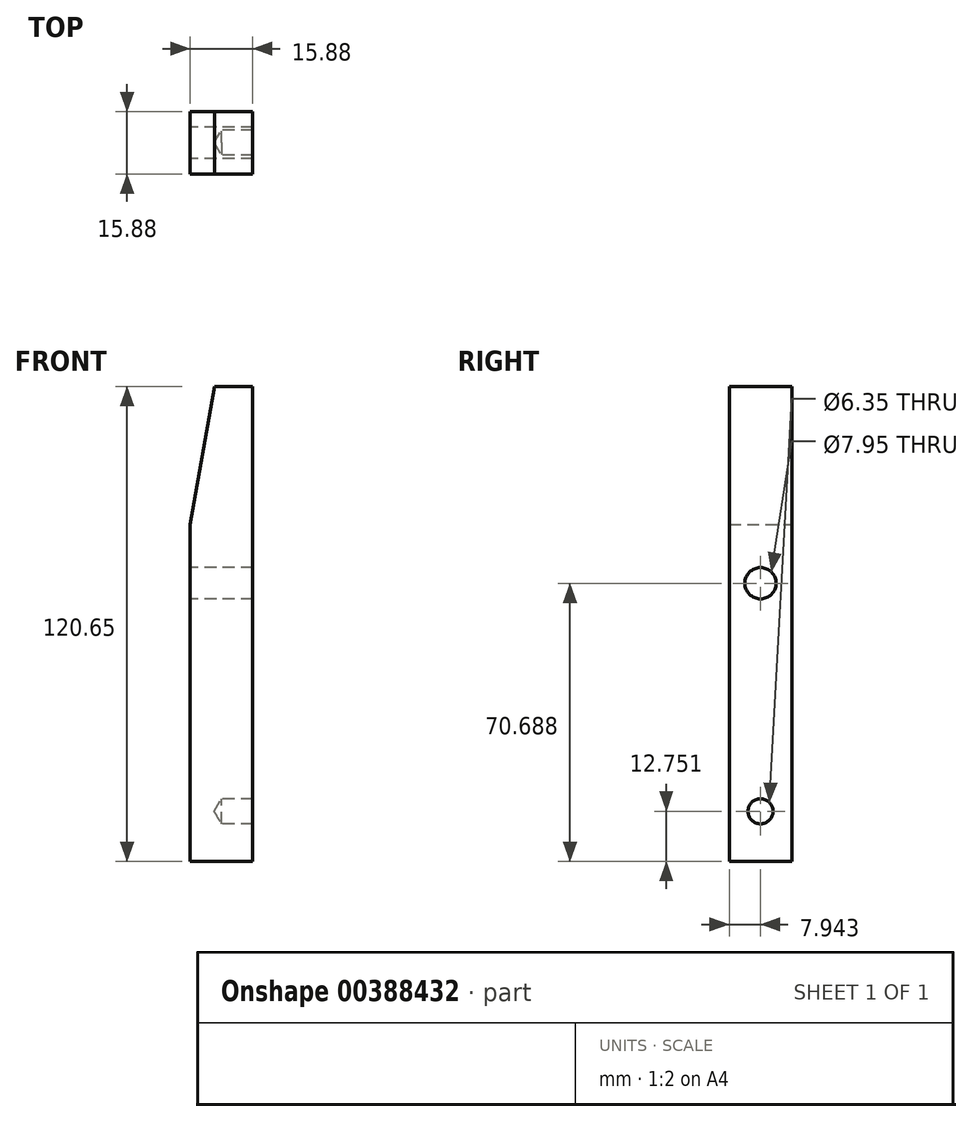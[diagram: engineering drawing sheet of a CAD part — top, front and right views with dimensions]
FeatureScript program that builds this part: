
annotation { "Feature Type Name" : "Feature", "Feature Type Description" : "" }
export const myFeature = defineFeature(function(context is Context, id is Id, definition is map)
    precondition{}
    {
        {
            var Q0;
            Q0=qCreatedBy(makeId("Front.planeOp"),FACE);
            var sketch = newSketch(context, id + "F0", { "sketchPlane" : qUnion([Q0])});
            skLineSegment(sketch, "E0", {"start": v(0, 0) * mm, "end": v(0, 85.6) * mm});
            skLineSegment(sketch, "E1", {"start": v(0, 85.6) * mm, "end": v(6.17, 120.65) * mm});
            skLineSegment(sketch, "E2", {"start": v(6.17, 120.65) * mm, "end": v(15.87, 120.65) * mm});
            skLineSegment(sketch, "E3", {"start": v(15.87, 120.65) * mm, "end": v(15.88, 0) * mm});
            skLineSegment(sketch, "E4", {"start": v(15.88, 0) * mm, "end": v(0, 0) * mm});
            skSolve(sketch);
        }
        {
            var Q0;
            Q0=makeQuery(id+"F0.imprint","IMPRINT",FACE,{"disambiguationData":[TD([[makeQuery(id+"F0.imprint","IMPRINT",EDGE,{"derivedFrom":sQuery(id+"F0.wireOp",EDGE,"E0")}),-1.0]])]});
            extrude(context, id + "F1", {"entities" : qUnion([Q0]), "depth" : 15.88 * mm});
        }
        {
            var Q0;
            Q0=makeQuery(id+"F1.opExtrude","SWEPT_FACE",FACE,{"disambiguationData":[OSD([sQuery(id+"F0.wireOp",EDGE,"E3")])]});
            var sketch = newSketch(context, id + "F2", { "sketchPlane" : qUnion([Q0])});
            skCircle(sketch, "E5", {"center": v(-7.94, 12.75) * mm, "radius": 3.18 * mm});
            skSolve(sketch);
        }
        {
            var Q0;
            Q0=sQuery(id+"F2.wireOp",VERTEX,"E5.center");
            var Q1;
            Q1=makeQuery(id+"F1.opExtrude","SWEPT_BODY",BODY,{"disambiguationData":[OSD([sQuery(id+"F0.wireOp",EDGE,"E0"),sQuery(id+"F0.wireOp",EDGE,"E1"),sQuery(id+"F0.wireOp",EDGE,"E2"),sQuery(id+"F0.wireOp",EDGE,"E3"),sQuery(id+"F0.wireOp",EDGE,"E4")])]});
            hole(context, id + "F3", {"style" : HoleStyle.SIMPLE, "endStyle" : HoleEndStyle.BLIND, "holeDiameter" : 6.35 * mm, "holeDepth" : 7.94 * mm, "isTappedThrough" : true, "tappedDepth" : 12.7 * mm, "tapClearance" : 3, "locations" : qUnion([Q0]), "scope" : qUnion([Q1])});
        }
        {
            var Q0;
            Q0=makeQuery(id+"F1.opExtrude","SWEPT_FACE",FACE,{"disambiguationData":[OSD([sQuery(id+"F0.wireOp",EDGE,"E3")])]});
            var sketch = newSketch(context, id + "F4", { "sketchPlane" : qUnion([Q0])});
            skLineSegment(sketch, "E6", {"start": v(-7.94, 120.65) * mm, "end": v(-7.94, 61.7) * mm, "construction": true});
            skLineSegment(sketch, "E7", {"start": v(-24.95, 70.69) * mm, "end": v(21.07, 70.69) * mm, "construction": true});
            skCircle(sketch, "E8", {"center": v(-7.94, 70.69) * mm, "radius": 3.98 * mm});
            skSolve(sketch);
        }
        {
            var Q0;
            Q0=sQuery(id+"F4.wireOp",VERTEX,"E8.center");
            var Q1;
            Q1=makeQuery(id+"F1.opExtrude","SWEPT_BODY",BODY,{"disambiguationData":[OSD([sQuery(id+"F0.wireOp",EDGE,"E0"),sQuery(id+"F0.wireOp",EDGE,"E1"),sQuery(id+"F0.wireOp",EDGE,"E2"),sQuery(id+"F0.wireOp",EDGE,"E3"),sQuery(id+"F0.wireOp",EDGE,"E4")])]});
            hole(context, id + "F5", {"style" : HoleStyle.SIMPLE, "endStyle" : HoleEndStyle.THROUGH, "holeDiameter" : 7.95 * mm, "isTappedThrough" : true, "tappedDepth" : 12.7 * mm, "tapClearance" : 3, "locations" : qUnion([Q0]), "scope" : qUnion([Q1])});
        }
    });
